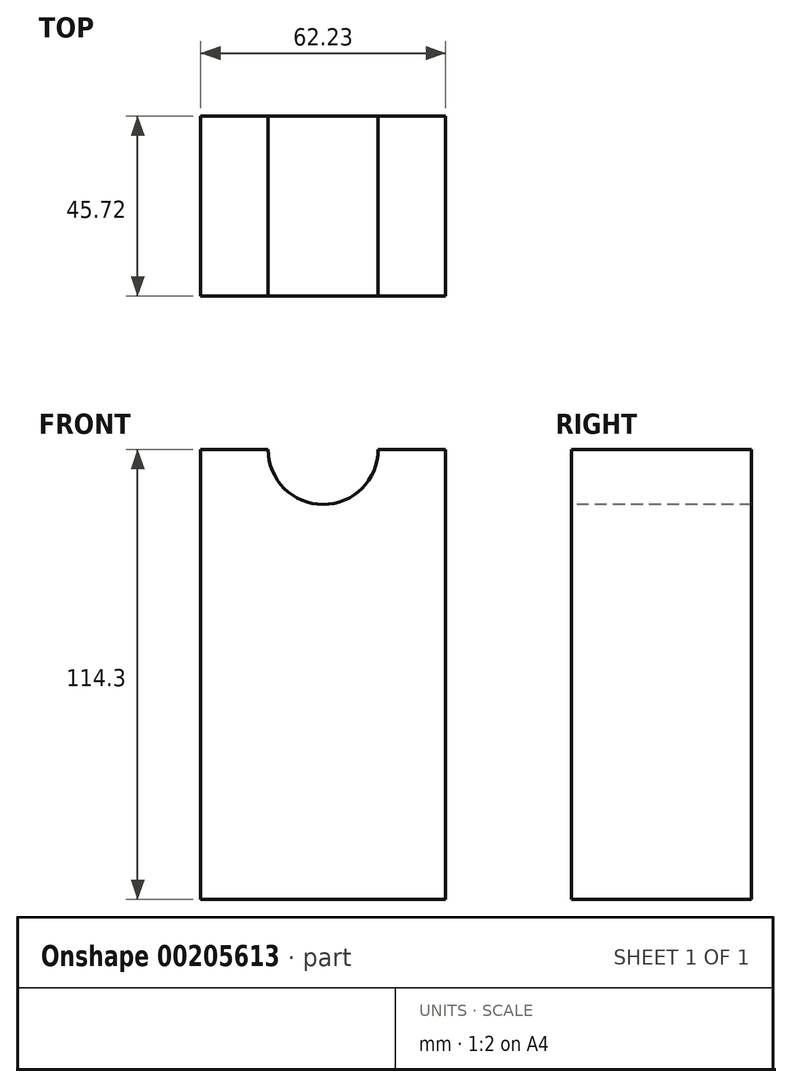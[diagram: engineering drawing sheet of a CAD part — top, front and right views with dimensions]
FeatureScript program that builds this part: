
annotation { "Feature Type Name" : "Feature", "Feature Type Description" : "" }
export const myFeature = defineFeature(function(context is Context, id is Id, definition is map)
    precondition{}
    {
        {
            var Q0;
            Q0=qCreatedBy(makeId("Front.planeOp"),FACE);
            var sketch = newSketch(context, id + "F0", { "sketchPlane" : qUnion([Q0])});
            skLineSegment(sketch, "E0", {"start": v(0, 0) * mm, "end": v(62.23, 0) * mm});
            skLineSegment(sketch, "E1", {"start": v(0, 0) * mm, "end": v(0, 114.3) * mm});
            skLineSegment(sketch, "E2", {"start": v(62.23, 0) * mm, "end": v(62.23, 114.3) * mm});
            skArc(sketch, "E3", {"start": v(17.14, 114.3) * mm, "mid": v(31.12, 100.33) * mm, "end": v(45.09, 114.3) * mm});
            skLineSegment(sketch, "E4", {"start": v(0, 114.3) * mm, "end": v(17.14, 114.3) * mm});
            skLineSegment(sketch, "E5", {"start": v(45.09, 114.3) * mm, "end": v(62.23, 114.3) * mm});
            skSolve(sketch);
        }
        {
            var Q0;
            Q0=makeQuery(id+"F0.imprint","IMPRINT",FACE,{"disambiguationData":[TD([[makeQuery(id+"F0.imprint","IMPRINT",EDGE,{"derivedFrom":sQuery(id+"F0.wireOp",EDGE,"E0")}),1.0]])]});
            extrude(context, id + "F1", {"entities" : qUnion([Q0]), "oppositeDirection" : true, "depth" : 45.72 * mm});
        }
    });
